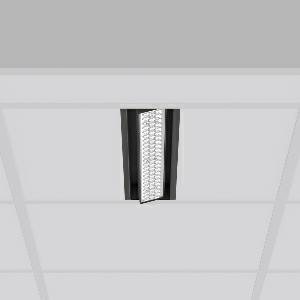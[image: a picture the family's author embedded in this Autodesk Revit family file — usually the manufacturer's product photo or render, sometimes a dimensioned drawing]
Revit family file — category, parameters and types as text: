
# Revit family: tx-move_901724_003_2_76_1e1a
name_source: partatom
category: Lighting Fixtures
units: mm (PartAtom-declared; Revit-internal decimal feet)

## family parameters
Cut with Voids When Loaded = No
Host = Face
Light Source = No
Part Type = Normal
Room Calculation Point = No
Round Connector Dimension = Use Diameter
Shared = No

## types (1)
- MultiLumen 1 (1 x LED Modul 927, 1950 lm, 2700)
    Apparent Load = 16 VA
    Approval mark = CE
    CIE Flux Codes = 88 96 99 100 100
    Color Rendering = 92
    Color Temperature = 2700
    Default Elevation = 1800 mm
    Description = Series: TX-MOVE
Einlege/Einbau-Flächenstrahler. Housing: sheet steel, powder-coated. Swivel range: 90°. High-efficiency LED units with optimum light control thanks to clear plastic (PC) lens optics. Spezielle Mikrostrukturen reduzieren Gelbsaum. Symmetrical light distribution. Best colour rendering with CRI >90 for fresh products and coloured textiles. Suitable for laying in grid ceiling module 600. Connected converter included in separate gearbox.Suitable for through-wiring.MultiLumen: Luminous flux adjustable in 3 steps. Accessories: Mounting frame for installation in suspended ceilings. Environmentally friendly and resource-saving due to replaceable and recyclable components. 
Colour: deep black, matt (RAL 9005)
Length: 597 mm
Width: 116 mm
Height: 39 mm
Cut-out length: 577 mm
Cut-out width: 98 mm
Recess height: 100 mm
Lamp: LED
Socket: without socket
Colour temperature: 2700K
Colour rendering index (CRI): 90
System power: 16 W
Rated luminous flux: 1950 lm
Luminous efficiency: 122 lm/W
System power 2: 23 W
Rated luminous flux 2: 2750 lm
Luminous efficiency 2: 120 lm/W
System power 3: 31 W
Rated luminous flux 3: 3500 lm
Luminous efficiency 3: 113 lm/W
Control gear: Dimmable EVG, DALI
Protection class: I
Type of protection: IP 20
    Height = 0 mm  [stored 0 ft]
    Lamp = 1 x LED Modul 927
    Lamp Light Flux = 1950 lm
    Lamp count = 1
    Length = 597 mm
    Lifetime = 50000 h
    Luminous efficacy = 122 lm/W
    Manufacturer = RZB
    ModVariant = No
    Model = 901724.003.2.76
    Mounting Place = Ceiling, Wall
    Mounting Type = Recessed
    Number of Poles = 1
    OnlyDefault = Yes
    Power Factor = 1
    Product Name = TX-MOVE
    Product group = Recessed projectors
    ProductGroupID = 401
    Protection Class = Protection class I
    Protection Degree = IP 20
    RLX_Detail_Level = 1
    RLX_Emergency_Light_Flux = 0 lm
    RLX_Emergency_Type = 0
    RLX_Emergency_Type_DB = No
    RlxData = <blob elided: 29557 chars, md5=eeaaa58d>
    Socket = socket
    Standby Power = 0 W
    System Light Flux = 1950 lm
    System Power = 16 W
    Type Comments = MultiLumen 1
    Type Image = 901725.003.jpg
    URL = http://relux.com
    VarID = multilumen_1
    Voltage = 230 V
    Voltage Range = 220-240 V
    Weight = 0.00 kg
    Width = 116 mm

note: [stored X ft] marks values corroborated as IEEE doubles in the binary element streams (Revit-internal decimal feet)

## geometry (parser evidence)
native form markers: Blend x4, Sweep x13
no freeform markers — native parametric forms only
